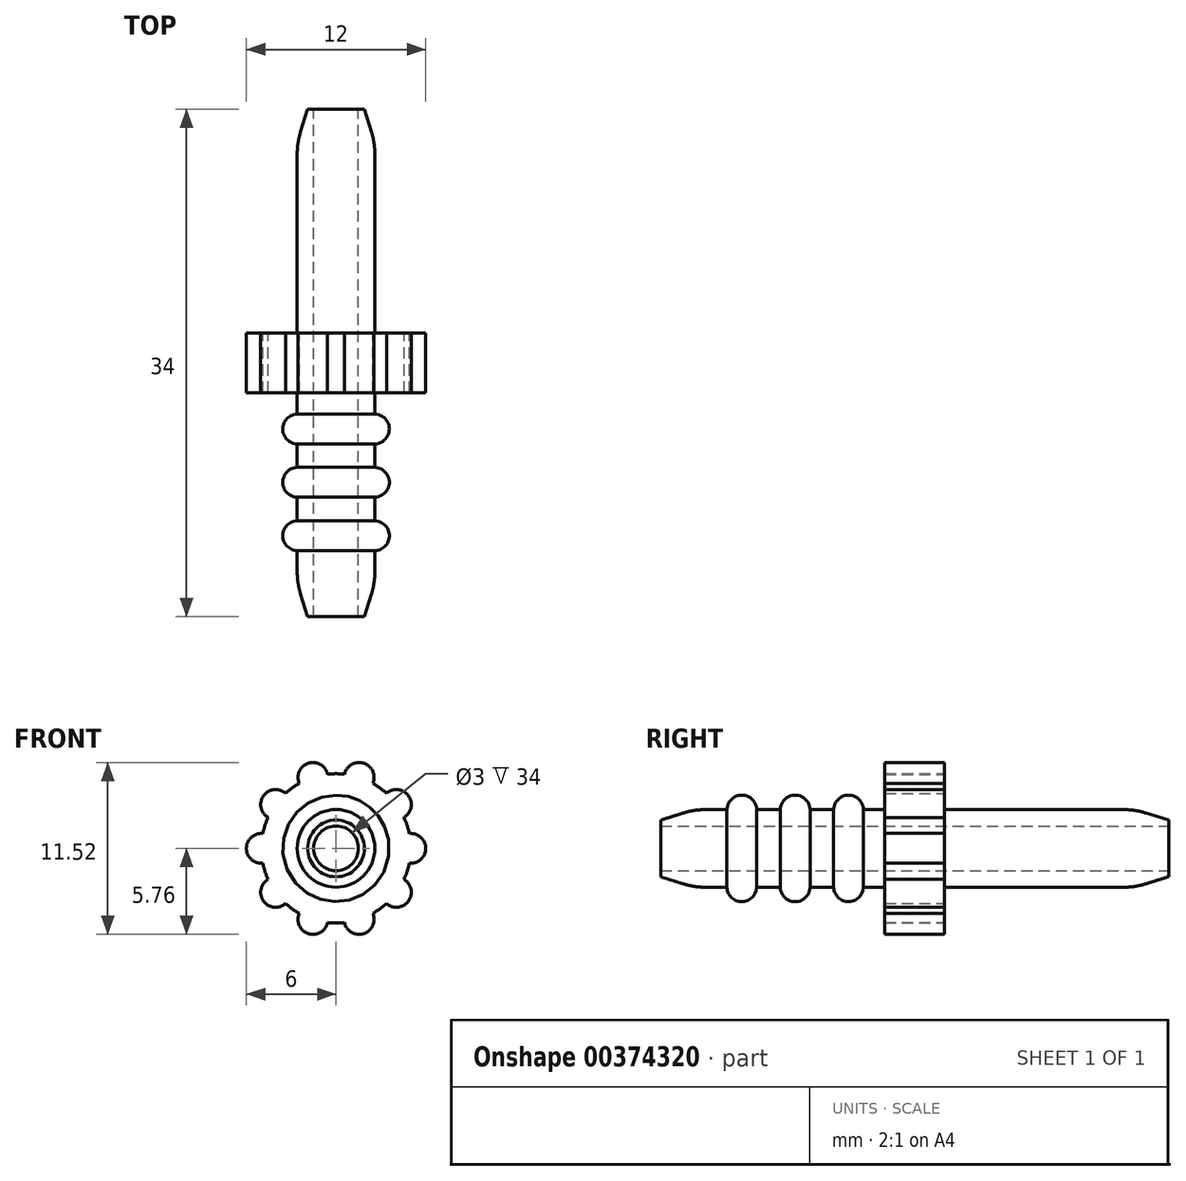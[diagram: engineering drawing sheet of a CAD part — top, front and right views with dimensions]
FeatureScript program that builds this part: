
annotation { "Feature Type Name" : "Feature", "Feature Type Description" : "" }
export const myFeature = defineFeature(function(context is Context, id is Id, definition is map)
    precondition{}
    {
        {
            var Q0;
            Q0=qCreatedBy(makeId("Front.planeOp"),FACE);
            var sketch = newSketch(context, id + "F0", { "sketchPlane" : qUnion([Q0])});
            skArc(sketch, "E0", {"start": v(-4.9, -1) * mm, "mid": v(-4.76, -1.55) * mm, "end": v(-4.55, -2.08) * mm});
            skCircle(sketch, "E1", {"center": v(0, 0) * mm, "radius": 2.6 * mm});
            skCircle(sketch, "E2", {"center": v(0, 0) * mm, "radius": 1.5 * mm});
            skArc(sketch, "E3", {"start": v(-4.9, 1) * mm, "mid": v(-6, 0) * mm, "end": v(-4.9, -1) * mm});
            skArc(sketch, "E4.1.0", {"start": v(-4.55, -2.08) * mm, "mid": v(-4.85, -3.53) * mm, "end": v(-3.38, -3.69) * mm});
            skArc(sketch, "E4.2.0", {"start": v(-2.46, -4.35) * mm, "mid": v(-1.85, -5.7) * mm, "end": v(-0.57, -4.97) * mm});
            skArc(sketch, "E4.3.0", {"start": v(0.57, -4.97) * mm, "mid": v(1.85, -5.7) * mm, "end": v(2.46, -4.35) * mm});
            skArc(sketch, "E4.4.0", {"start": v(3.38, -3.69) * mm, "mid": v(4.85, -3.53) * mm, "end": v(4.55, -2.08) * mm});
            skArc(sketch, "E4.5.0", {"start": v(4.9, -1) * mm, "mid": v(6, 0) * mm, "end": v(4.9, 1) * mm});
            skArc(sketch, "E4.6.0", {"start": v(4.55, 2.08) * mm, "mid": v(4.85, 3.53) * mm, "end": v(3.38, 3.69) * mm});
            skArc(sketch, "E4.7.0", {"start": v(2.46, 4.35) * mm, "mid": v(1.85, 5.7) * mm, "end": v(0.57, 4.97) * mm});
            skArc(sketch, "E4.8.0", {"start": v(-0.57, 4.97) * mm, "mid": v(-1.85, 5.7) * mm, "end": v(-2.46, 4.35) * mm});
            skArc(sketch, "E4.9.0", {"start": v(-3.38, 3.69) * mm, "mid": v(-4.85, 3.53) * mm, "end": v(-4.55, 2.08) * mm});
            skArc(sketch, "E5.trimOffspring", {"start": v(-4.55, 2.08) * mm, "mid": v(-4.76, 1.55) * mm, "end": v(-4.9, 1) * mm});
            skArc(sketch, "E6.trimOffspring", {"start": v(-2.46, 4.35) * mm, "mid": v(-2.94, 4.05) * mm, "end": v(-3.38, 3.69) * mm});
            skArc(sketch, "E7.trimOffspring", {"start": v(0.57, 4.97) * mm, "mid": v(0, 5) * mm, "end": v(-0.57, 4.97) * mm});
            skArc(sketch, "E8.trimOffspring", {"start": v(3.38, 3.69) * mm, "mid": v(2.94, 4.05) * mm, "end": v(2.46, 4.35) * mm});
            skArc(sketch, "E9.trimOffspring", {"start": v(4.9, 1) * mm, "mid": v(4.76, 1.55) * mm, "end": v(4.55, 2.08) * mm});
            skArc(sketch, "E10.trimOffspring", {"start": v(4.55, -2.08) * mm, "mid": v(4.76, -1.55) * mm, "end": v(4.9, -1) * mm});
            skArc(sketch, "E11.trimOffspring", {"start": v(2.46, -4.35) * mm, "mid": v(2.94, -4.05) * mm, "end": v(3.38, -3.69) * mm});
            skArc(sketch, "E12.trimOffspring", {"start": v(-0.57, -4.97) * mm, "mid": v(0, -5) * mm, "end": v(0.57, -4.97) * mm});
            skArc(sketch, "E13.trimOffspring", {"start": v(-3.38, -3.69) * mm, "mid": v(-2.94, -4.05) * mm, "end": v(-2.46, -4.35) * mm});
            skSolve(sketch);
        }
        {
            var Q0;
            Q0=makeQuery(id+"F0.imprint","IMPRINT",FACE,{"disambiguationData":[TD([[makeQuery(id+"F0.imprint","IMPRINT",EDGE,{"derivedFrom":sQuery(id+"F0.wireOp",EDGE,"E1")}),1.0]])]});
            extrude(context, id + "F1", {"entities" : qUnion([Q0]), "endBound" : BoundingType.SYMMETRIC, "depth" : 34 * mm});
        }
        {
            var Q0;
            Q0=makeQuery(id+"F0.imprint","IMPRINT",FACE,{"disambiguationData":[TD([[makeQuery(id+"F0.imprint","IMPRINT",EDGE,{"derivedFrom":sQuery(id+"F0.wireOp",EDGE,"E0")}),1.0]])]});
            extrude(context, id + "F2", {"entities" : qUnion([Q0]), "operationType" : NewBodyOperationType.ADD, "endBound" : BoundingType.SYMMETRIC, "depth" : 4 * mm});
        }
        {
            var Q0;
            Q0=qCreatedBy(makeId("Right.planeOp"),FACE);
            var sketch = newSketch(context, id + "F3", { "sketchPlane" : qUnion([Q0])});
            skLineSegment(sketch, "E14", {"start": v(0, 11.47) * mm, "end": v(0, -11.3) * mm});
            skLineSegment(sketch, "E15", {"start": v(18.86, 0) * mm, "end": v(-23.14, 0) * mm});
            skCircle(sketch, "E16", {"center": v(-11.57, 2.57) * mm, "radius": 1 * mm});
            skCircle(sketch, "E17", {"center": v(-8, 2.57) * mm, "radius": 1 * mm});
            skCircle(sketch, "E18", {"center": v(-4.42, 2.57) * mm, "radius": 1 * mm});
            skCircle(sketch, "E19.MirrorC", {"center": v(4.42, 2.57) * mm, "radius": 1 * mm});
            skCircle(sketch, "E20.MirrorC", {"center": v(8, 2.57) * mm, "radius": 1 * mm});
            skCircle(sketch, "E21.MirrorC", {"center": v(11.57, 2.57) * mm, "radius": 1 * mm});
            skSolve(sketch);
        }
        {
            var Q0;
            Q0=makeQuery(id+"F3.imprint","IMPRINT",FACE,{"disambiguationData":[TD([[makeQuery(id+"F3.imprint","IMPRINT",EDGE,{"derivedFrom":sQuery(id+"F3.wireOp",EDGE,"E16")}),1.0]])]});
            var Q1;
            Q1=makeQuery(id+"F3.imprint","IMPRINT",FACE,{"disambiguationData":[TD([[makeQuery(id+"F3.imprint","IMPRINT",EDGE,{"derivedFrom":sQuery(id+"F3.wireOp",EDGE,"E17")}),1.0]])]});
            var Q2;
            Q2=makeQuery(id+"F3.imprint","IMPRINT",FACE,{"disambiguationData":[TD([[makeQuery(id+"F3.imprint","IMPRINT",EDGE,{"derivedFrom":sQuery(id+"F3.wireOp",EDGE,"E18")}),1.0]])]});
            var Q3;
            Q3=makeQuery(id+"F3.imprint","IMPRINT",FACE,{"disambiguationData":[TD([[makeQuery(id+"F3.imprint","IMPRINT",EDGE,{"derivedFrom":sQuery(id+"F3.wireOp",EDGE,"E19.MirrorC")}),-1.0]])]});
            var Q4;
            Q4=makeQuery(id+"F3.imprint","IMPRINT",FACE,{"disambiguationData":[TD([[makeQuery(id+"F3.imprint","IMPRINT",EDGE,{"derivedFrom":sQuery(id+"F3.wireOp",EDGE,"E20.MirrorC")}),-1.0]])]});
            var Q5;
            Q5=makeQuery(id+"F3.imprint","IMPRINT",FACE,{"disambiguationData":[TD([[makeQuery(id+"F3.imprint","IMPRINT",EDGE,{"derivedFrom":sQuery(id+"F3.wireOp",EDGE,"E21.MirrorC")}),-1.0]])]});
            var Q6;
            Q6=sQuery(id+"F3.wireOp",EDGE,"E15");
            revolve(context, id + "F4", {"operationType" : NewBodyOperationType.ADD, "entities" : qUnion([Q0, Q1, Q2, Q3, Q4, Q5]), "axis" : qUnion([Q6]), "revolveType" : RevolveType.FULL});
        }
        {
            var Q0;
            Q0=qCreatedBy(makeId("Right.planeOp"),FACE);
            var sketch = newSketch(context, id + "F5", { "sketchPlane" : qUnion([Q0])});
            skLineSegment(sketch, "E22", {"start": v(-20.11, 0) * mm, "end": v(19.82, 0) * mm});
            skLineSegment(sketch, "E23", {"start": v(-18.83, 1.33) * mm, "end": v(-18.83, 3.02) * mm});
            skLineSegment(sketch, "E24", {"start": v(-18.83, 3.02) * mm, "end": v(-13.38, 3.02) * mm});
            skLineSegment(sketch, "E25", {"start": v(-13.38, 3.02) * mm, "end": v(-18.83, 1.33) * mm});
            skLineSegment(sketch, "E26", {"start": v(0, 9.55) * mm, "end": v(0, -10) * mm});
            skLineSegment(sketch, "E27.MirrorCS", {"start": v(18.83, 3.02) * mm, "end": v(13.38, 3.02) * mm});
            skLineSegment(sketch, "E28.MirrorCS", {"start": v(13.38, 3.02) * mm, "end": v(18.83, 1.33) * mm});
            skLineSegment(sketch, "E29.MirrorCS", {"start": v(18.83, 1.33) * mm, "end": v(18.83, 3.02) * mm});
            skSolve(sketch);
        }
        {
            var Q0;
            Q0=makeQuery(id+"F5.imprint","IMPRINT",FACE,{"disambiguationData":[TD([[makeQuery(id+"F5.imprint","IMPRINT",EDGE,{"derivedFrom":sQuery(id+"F5.wireOp",EDGE,"E23")}),-1.0]])]});
            var Q1;
            Q1=makeQuery(id+"F5.imprint","IMPRINT",FACE,{"disambiguationData":[TD([[makeQuery(id+"F5.imprint","IMPRINT",EDGE,{"derivedFrom":sQuery(id+"F5.wireOp",EDGE,"E27.MirrorCS")}),1.0]])]});
            var Q2;
            Q2=sQuery(id+"F5.wireOp",EDGE,"E22");
            revolve(context, id + "F6", {"operationType" : NewBodyOperationType.REMOVE, "entities" : qUnion([Q0, Q1]), "axis" : qUnion([Q2]), "revolveType" : RevolveType.FULL, "oppositeDirection" : true});
        }
        {
            var Q0;
            {var subQ0=sQuery(id+"F0.wireOp",EDGE,"E1");var subQ1=makeQuery(id+"F1.opExtrude","CAP_FACE",FACE,{"disambiguationData":[OSD([subQ0,sQuery(id+"F0.wireOp",EDGE,"E2")])],"isStart":true});Q0=makeQuery(id+"F6.boolean.opBoolean","INTERSECT",EDGE,{"derivedFrom":[makeQuery(id+"F4.boolean.opBoolean","SPLIT",FACE,{"disambiguationData":[TD([subQ1,makeQuery(id+"F4.opRevolve","SWEPT_FACE",FACE,{"disambiguationData":[OSD([sQuery(id+"F3.wireOp",EDGE,"E21.MirrorC")])]})])],"derivedFrom":makeQuery(id+"F2.boolean.opBoolean","SPLIT",FACE,{"disambiguationData":[TD([subQ1])],"derivedFrom":makeQuery(id+"F1.opExtrude","SWEPT_FACE",FACE,{"disambiguationData":[OSD([subQ0])]})})}),makeQuery(id+"F6.opRevolve","SWEPT_FACE",FACE,{"disambiguationData":[OSD([sQuery(id+"F5.wireOp",EDGE,"E28.MirrorCS")])]})]});}
            var Q1;
            {var subQ0=sQuery(id+"F0.wireOp",EDGE,"E1");var subQ1=makeQuery(id+"F1.opExtrude","CAP_FACE",FACE,{"disambiguationData":[OSD([subQ0,sQuery(id+"F0.wireOp",EDGE,"E2")])],"isStart":false});Q1=makeQuery(id+"F6.boolean.opBoolean","INTERSECT",EDGE,{"derivedFrom":[makeQuery(id+"F4.boolean.opBoolean","SPLIT",FACE,{"disambiguationData":[TD([subQ1,makeQuery(id+"F4.opRevolve","SWEPT_FACE",FACE,{"disambiguationData":[OSD([sQuery(id+"F3.wireOp",EDGE,"E16")])]})])],"derivedFrom":makeQuery(id+"F2.boolean.opBoolean","SPLIT",FACE,{"disambiguationData":[TD([subQ1])],"derivedFrom":makeQuery(id+"F1.opExtrude","SWEPT_FACE",FACE,{"disambiguationData":[OSD([subQ0])]})})}),makeQuery(id+"F6.opRevolve","SWEPT_FACE",FACE,{"disambiguationData":[OSD([sQuery(id+"F5.wireOp",EDGE,"E25")])]})]});}
            fillet(context, id + "F7", {"entities" : qUnion([Q0, Q1]), "radius" : 5 * mm, "tangentPropagation" : true, "allowEdgeOverflow" : false});
        }
    });
